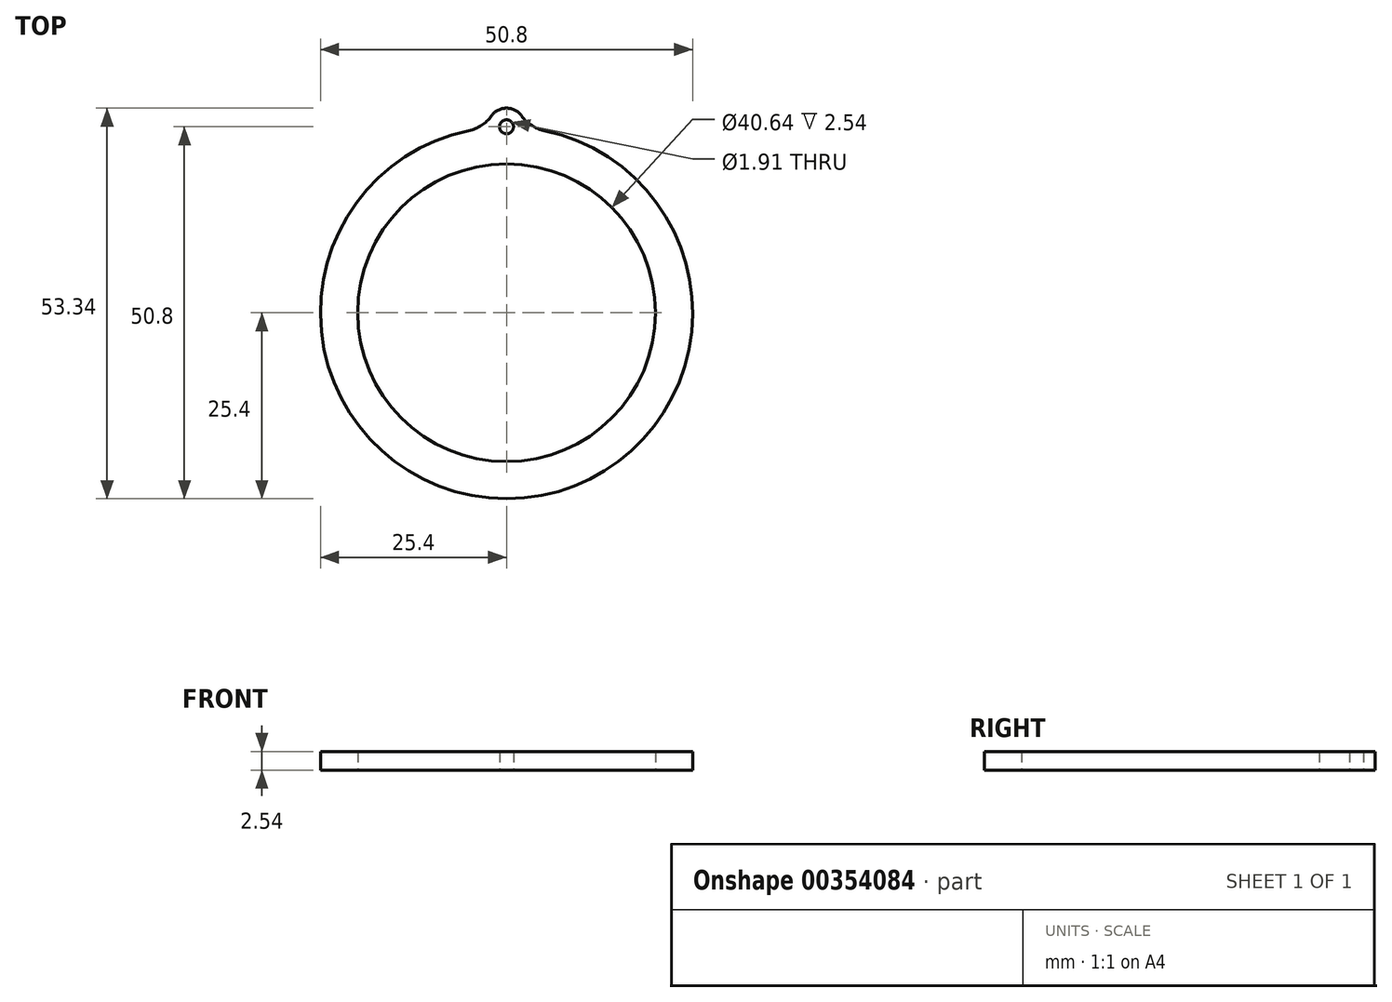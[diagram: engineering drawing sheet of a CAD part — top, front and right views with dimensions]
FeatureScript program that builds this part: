
annotation { "Feature Type Name" : "Feature", "Feature Type Description" : "" }
export const myFeature = defineFeature(function(context is Context, id is Id, definition is map)
    precondition{}
    {
        {
            var Q0;
            Q0=qCreatedBy(makeId("Top.planeOp"),FACE);
            var sketch = newSketch(context, id + "F0", { "sketchPlane" : qUnion([Q0])});
            skArc(sketch, "E0", {"start": v(-2.54, 25.27) * mm, "mid": v(0, -25.4) * mm, "end": v(2.54, 25.27) * mm});
            skCircle(sketch, "E1", {"center": v(0, 0) * mm, "radius": 20.32 * mm});
            skArc(sketch, "E2", {"start": v(2.54, 25.27) * mm, "mid": v(0, 27.94) * mm, "end": v(-2.54, 25.27) * mm});
            skCircle(sketch, "E3", {"center": v(0, 25.4) * mm, "radius": 0.95 * mm});
            skSolve(sketch);
        }
        {
            var Q0;
            Q0 = qSketchRegion(id + "F0", true);
            extrude(context, id + "F1", {"entities" : qUnion([Q0]), "depth" : 2.54 * mm});
        }
        {
            var Q0;
            {var subQ0=sQuery(id+"F0.wireOp",EDGE,"E2");var subQ1=sQuery(id+"F0.wireOp",EDGE,"E0");Q0=makeQuery(id+"F1.opExtrude","SWEPT_EDGE",EDGE,{"disambiguationData":[OSD([subQ1,subQ0]),TDD([makeQuery(id+"F0.imprint","INTERSECT",VERTEX,{"disambiguationData":[OD(1.0)],"derivedFrom":[subQ1,subQ0]})])]});}
            var Q1;
            {var subQ0=sQuery(id+"F0.wireOp",EDGE,"E2");var subQ1=sQuery(id+"F0.wireOp",EDGE,"E0");Q1=makeQuery(id+"F1.opExtrude","SWEPT_EDGE",EDGE,{"disambiguationData":[OSD([subQ1,subQ0]),TDD([makeQuery(id+"F0.imprint","INTERSECT",VERTEX,{"disambiguationData":[OD(0.0)],"derivedFrom":[subQ1,subQ0]})])]});}
            fillet(context, id + "F2", {"entities" : qUnion([Q0, Q1]), "radius" : 5.08 * mm, "tangentPropagation" : true, "allowEdgeOverflow" : false});
        }
    });
